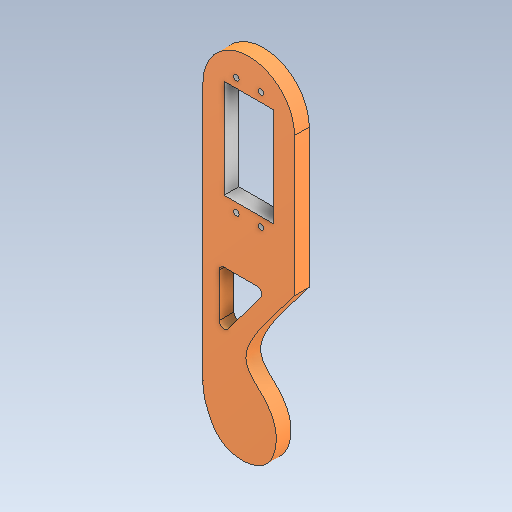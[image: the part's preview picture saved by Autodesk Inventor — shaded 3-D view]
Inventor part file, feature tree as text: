
AUTODESK INVENTOR PART (.ipt)
format: ipt  version: 2020.3 (Build 243373000, 373)  size: 209,408 bytes
history: native  units: mm
features: other x3, extrude x2, sketch x2, direct_edit x1, projected_geometry x1, move_body x1
ambient origin geometry x8: Origin, YZ Plane, XZ Plane, XY Plane, X Axis, Y Axis, Z Axis, Center Point
bodies: Solid1 (feature_tree)
feature tree (10):
  other  "Part 6.ipt"
  extrude  "Extrusion1"  Depth=10.0mm TaperAngle=0.0deg
  sketch  "Sketch2"  dims[d3=0.0mm d4=-5.25mm d5=0.0mm d6=0.0mm d7=0.0mm]
  direct_edit  "Direct Edit1"
  extrude  "Extrusion2"  TaperAngle=0.0deg  [1 undecoded]
  other  "Solid1::Part 6.ipt"
  other  "TaggingFeature1"
  sketch  "Sketch1"  dims[d0=20.0mm d1=10.0mm d2=0.0mm]
  projected_geometry  "Projected Loop1"
  move_body  "Move1"
note: 1 required parameter value undecoded (feature->parameter linkage not recoverable at this tier; creation-order binding heuristic only, values carry confidence <= 0.55)
